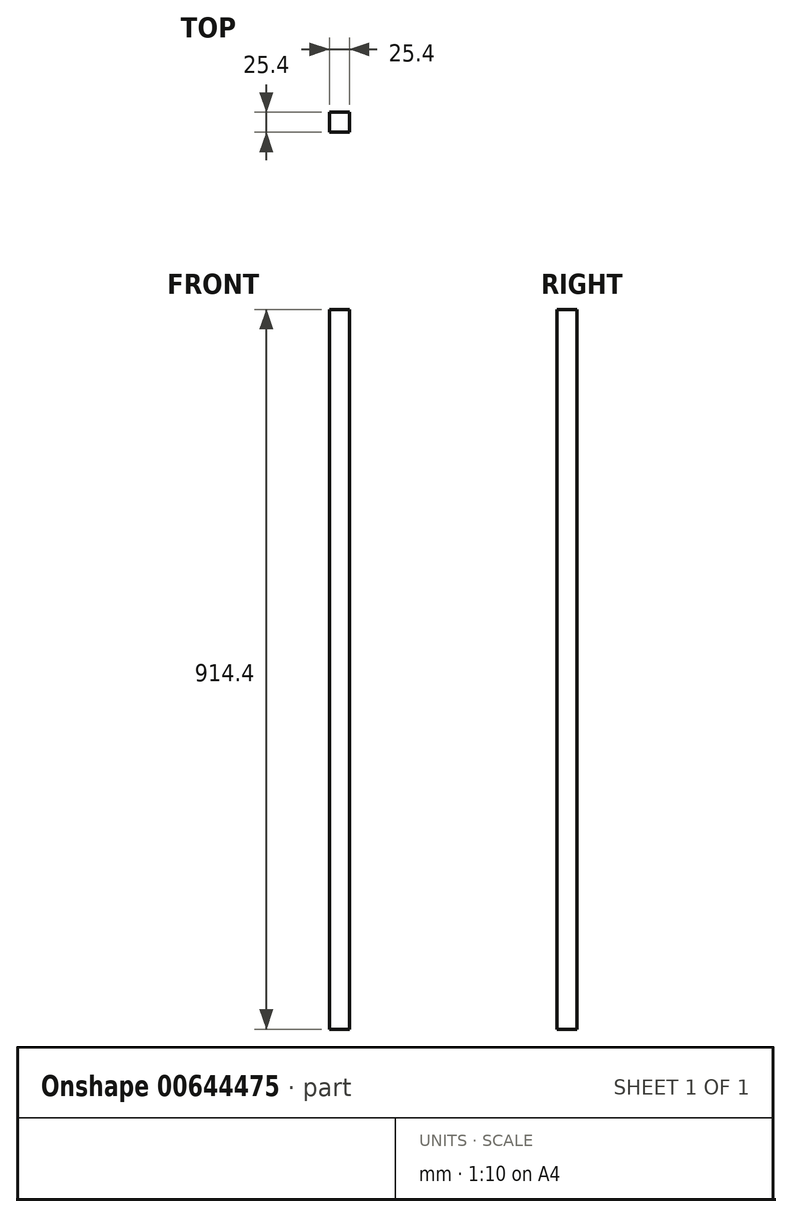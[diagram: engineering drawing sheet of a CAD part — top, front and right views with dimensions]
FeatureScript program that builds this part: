
annotation { "Feature Type Name" : "Feature", "Feature Type Description" : "" }
export const myFeature = defineFeature(function(context is Context, id is Id, definition is map)
    precondition{}
    {
        {
            var Q0;
            Q0=qCreatedBy(makeId("Top.planeOp"),FACE);
            var sketch = newSketch(context, id + "F0", { "sketchPlane" : qUnion([Q0])});
            skLineSegment(sketch, "E0.bottom", {"start": v(-13.58, 15.92) * mm, "end": v(11.82, 15.92) * mm});
            skLineSegment(sketch, "E0.top", {"start": v(-13.58, -9.48) * mm, "end": v(11.82, -9.48) * mm});
            skLineSegment(sketch, "E0.left", {"start": v(-13.58, 15.92) * mm, "end": v(-13.58, -9.48) * mm});
            skLineSegment(sketch, "E0.right", {"start": v(11.82, 15.92) * mm, "end": v(11.82, -9.48) * mm});
            skSolve(sketch);
        }
        {
            var Q0;
            Q0 = qSketchRegion(id + "F0", true);
            extrude(context, id + "F1", {"entities" : qUnion([Q0]), "endBound" : BoundingType.SYMMETRIC, "oppositeDirection" : true, "depth" : 914.4 * mm, "offsetDistance" : 25.4 * mm});
        }
    });
